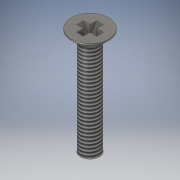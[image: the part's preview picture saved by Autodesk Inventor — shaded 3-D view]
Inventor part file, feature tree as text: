
AUTODESK INVENTOR PART (.ipt)
format: ipt  version: 2019 (Build 230136000, 136)  size: 137,216 bytes
history: native  units: mm
features: sketch x2, other x1, revolve x1, extrude x1, pattern_circular x1, thread x1
ambient origin geometry x8: Origin, YZ Plane, XZ Plane, XY Plane, X Axis, Y Axis, Z Axis, Center Point
bodies: Body1 (feature_tree)
feature tree (7):
  other  "Твердое тело1"
  revolve  "Вращение1"
  extrude  "Выдавливание1"  Depth=2.8mm
  pattern_circular  "Круговой массив1"  Angle=45.0deg  [1 undecoded]
  thread  "Резьба1"
  sketch  "Эскиз1"
  sketch  "Эскиз2"
note: 1 required parameter value undecoded (feature->parameter linkage not recoverable at this tier; creation-order binding heuristic only, values carry confidence <= 0.55)
